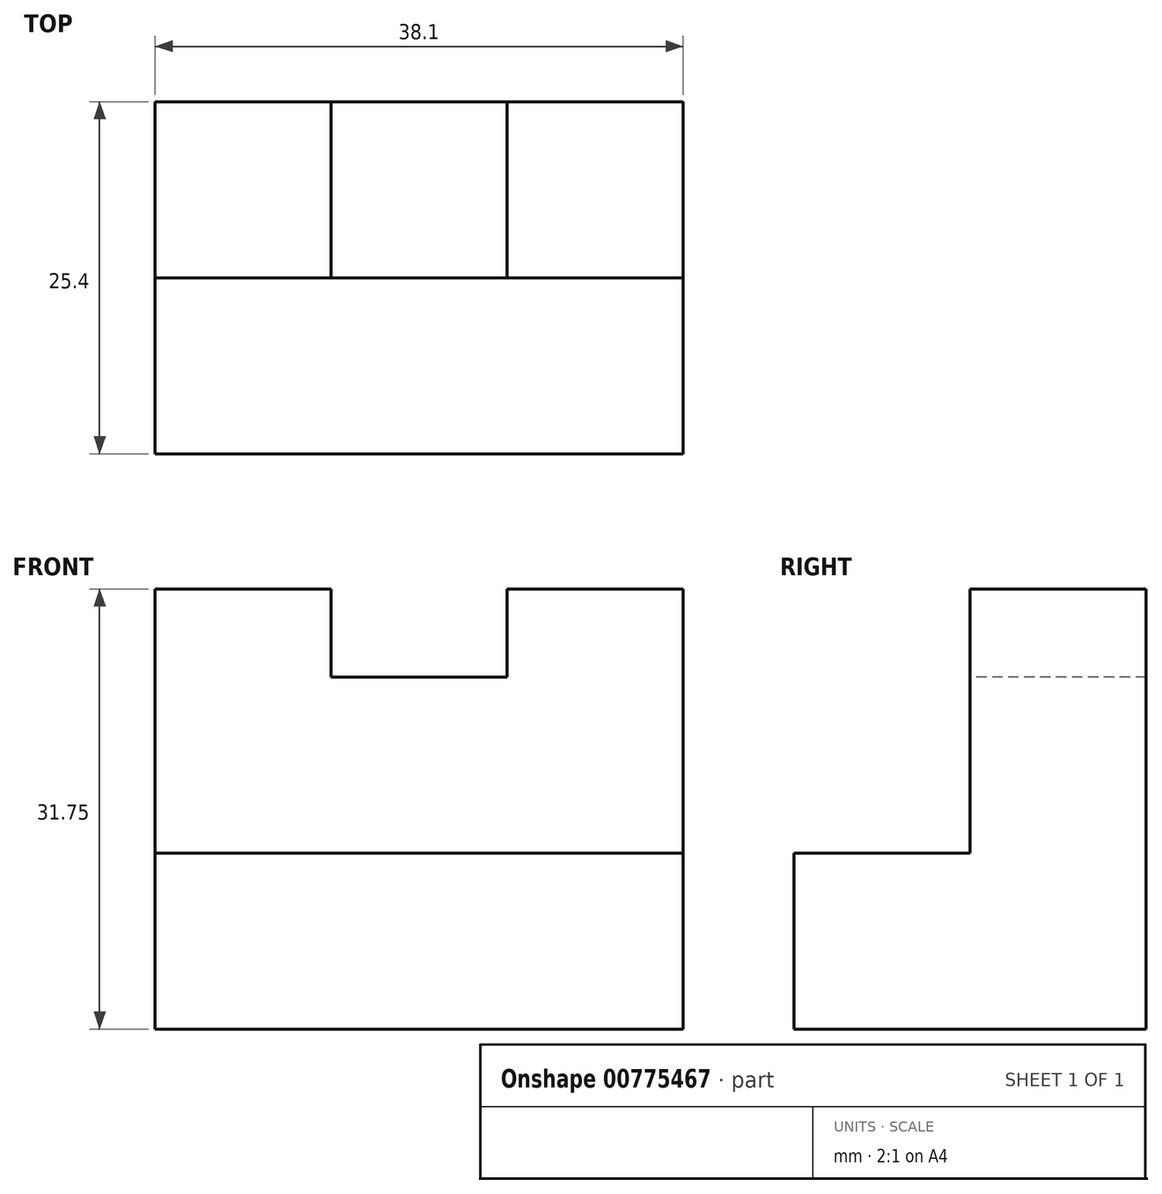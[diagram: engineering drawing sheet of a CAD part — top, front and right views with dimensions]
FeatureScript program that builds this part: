
annotation { "Feature Type Name" : "Feature", "Feature Type Description" : "" }
export const myFeature = defineFeature(function(context is Context, id is Id, definition is map)
    precondition{}
    {
        {
            var Q0;
            Q0=qCreatedBy(makeId("Front.planeOp"),FACE);
            var sketch = newSketch(context, id + "F0", { "sketchPlane" : qUnion([Q0])});
            skLineSegment(sketch, "E0", {"start": v(0, 0) * mm, "end": v(38.1, 0) * mm});
            skLineSegment(sketch, "E1", {"start": v(38.1, 0) * mm, "end": v(38.1, 31.75) * mm});
            skLineSegment(sketch, "E2", {"start": v(38.1, 31.75) * mm, "end": v(0, 31.75) * mm});
            skLineSegment(sketch, "E3", {"start": v(0, 31.75) * mm, "end": v(0, 0) * mm});
            skSolve(sketch);
        }
        {
            var Q0;
            Q0=makeQuery(id+"F0.imprint","IMPRINT",FACE,{"disambiguationData":[TD([[makeQuery(id+"F0.imprint","IMPRINT",EDGE,{"derivedFrom":sQuery(id+"F0.wireOp",EDGE,"E0")}),1.0]])]});
            extrude(context, id + "F1", {"entities" : qUnion([Q0]), "depth" : 25.4 * mm, "offsetDistance" : 25.4 * mm});
        }
        {
            var Q0;
            Q0=makeQuery(id+"F1.opExtrude","SWEPT_FACE",FACE,{"disambiguationData":[OSD([sQuery(id+"F0.wireOp",EDGE,"E1")])]});
            var sketch = newSketch(context, id + "F2", { "sketchPlane" : qUnion([Q0])});
            skLineSegment(sketch, "E4", {"start": v(-25.4, 0) * mm, "end": v(-25.4, 12.7) * mm});
            skLineSegment(sketch, "E5", {"start": v(-25.4, 12.7) * mm, "end": v(-12.7, 12.7) * mm});
            skLineSegment(sketch, "E6", {"start": v(0, 31.75) * mm, "end": v(-12.7, 31.75) * mm});
            skLineSegment(sketch, "E7", {"start": v(-12.7, 31.75) * mm, "end": v(-12.7, 12.7) * mm});
            skSolve(sketch);
        }
        {
            var Q0;
            {var subQ0=sQuery(id+"F2.wireOp",EDGE,"E5");Q0=makeQuery(id+"F2.imprint","IMPRINT",FACE,{"disambiguationData":[TD([[makeQuery(id+"F2.imprint","IMPRINT",EDGE,{"derivedFrom":subQ0}),1.0]])]});}
            extrude(context, id + "F3", {"entities" : qUnion([Q0]), "operationType" : NewBodyOperationType.REMOVE, "oppositeDirection" : true, "depth" : 38.1 * mm, "offsetDistance" : 25.4 * mm});
        }
        {
            var Q0;
            Q0=makeQuery(id+"F3.boolean.opBoolean","COPY",FACE,{"derivedFrom":makeQuery(id+"F3.opExtrude","SWEPT_FACE",FACE,{"disambiguationData":[OSD([sQuery(id+"F2.wireOp",EDGE,"E7")])]})});
            var sketch = newSketch(context, id + "F4", { "sketchPlane" : qUnion([Q0])});
            skLineSegment(sketch, "E8", {"start": v(0, 31.75) * mm, "end": v(12.7, 31.75) * mm});
            skLineSegment(sketch, "E9", {"start": v(12.7, 31.75) * mm, "end": v(12.7, 25.4) * mm});
            skLineSegment(sketch, "E10", {"start": v(12.7, 25.4) * mm, "end": v(25.4, 25.4) * mm});
            skLineSegment(sketch, "E11", {"start": v(25.4, 25.4) * mm, "end": v(25.4, 31.75) * mm});
            skSolve(sketch);
        }
        {
            var Q0;
            {var subQ0=sQuery(id+"F4.wireOp",EDGE,"E9");Q0=makeQuery(id+"F4.imprint","IMPRINT",FACE,{"disambiguationData":[TD([[makeQuery(id+"F4.imprint","IMPRINT",EDGE,{"derivedFrom":subQ0}),1.0]])]});}
            extrude(context, id + "F5", {"entities" : qUnion([Q0]), "operationType" : NewBodyOperationType.REMOVE, "oppositeDirection" : true, "depth" : 12.7 * mm, "offsetDistance" : 25.4 * mm});
        }
    });
